# Revit family: Deca_Cuba de cozinha_Wish_CC.610.40.STD
name_source: partatom
category: Plumbing Fixtures
units: mm (PartAtom-declared; Revit-internal decimal feet)

## family parameters
Cut with Voids When Loaded = Yes
Host = Face
Part Type = Normal
Room Calculation Point = No
Round Connector Dimension = Use Radius
Shared = No

## types (1)
- CC.610.40.STD.INX_Inox
    Acompanha o Produto = Acompanha Bisnaga de Silicone; parafuso, grampo e suporte para fixação; Kit Sifão e Valvula de Escoamento e válvula escoamento com mangueira do ladrão; Pop Pap
    Aprovado por = quattroD
    Atendimento ao Cliente = 0800-0117073
    Categoria = CUBAS COZINHA
    Composição Anel Vedação = -
    Composição Assento = -
    Composição Básica = Aço Inoxidável
    Composição Componente = -
    Consumo = -
    Cor Interna = -
    Cor Principal = Inox
    Cor Secundária = -
    Cores Componente = -
    Criado por = quattroD
    Código Pai = CC.610.40.STD
    Default Elevation = 0 mm  [stored 0 ft]
    Description = Cuba de cozinha
    Diâmetro Ponto de Esgoto = 25 mm  [stored 0.082021 ft]
    Informações Complementares = -
    Itens de Instalação = -
    Linha = Cubas de Cozinha
    Manufacturer = Deca
    Material = Deca_Inox
    Model = CC.610.40.STD.INX
    Norma = Não Possui
    Peso Líquido (Kg) = 4.45
    Pressão máx. funcionamento = -
    Pressão mín. Aquec. Acúmulo = -
    Pressão mín. Aquec. Passagem = -
    Pressão mín. funcionamento = -
    Raio Ponto de Esgoto = 13 mm  [stored 0.0426509 ft]
    Saída de Esgoto = -
    Segmento = Cozinha Luxo
    Tipo de dispositivo economizador = -
    Tipo de mecanismo utilizado = -
    Tipo de rosca de entrada = -
    Tipo de rosca de saída = -
    URL = www.deca.com.br
    Vazão na Pressão máx. (L/min) = -
    Vazão na Pressão mín. (L/min) = -

note: [stored X ft] marks values corroborated as IEEE doubles in the binary element streams (Revit-internal decimal feet)

## geometry (parser evidence)
native form markers: Sweep x2
no freeform markers — native parametric forms only
